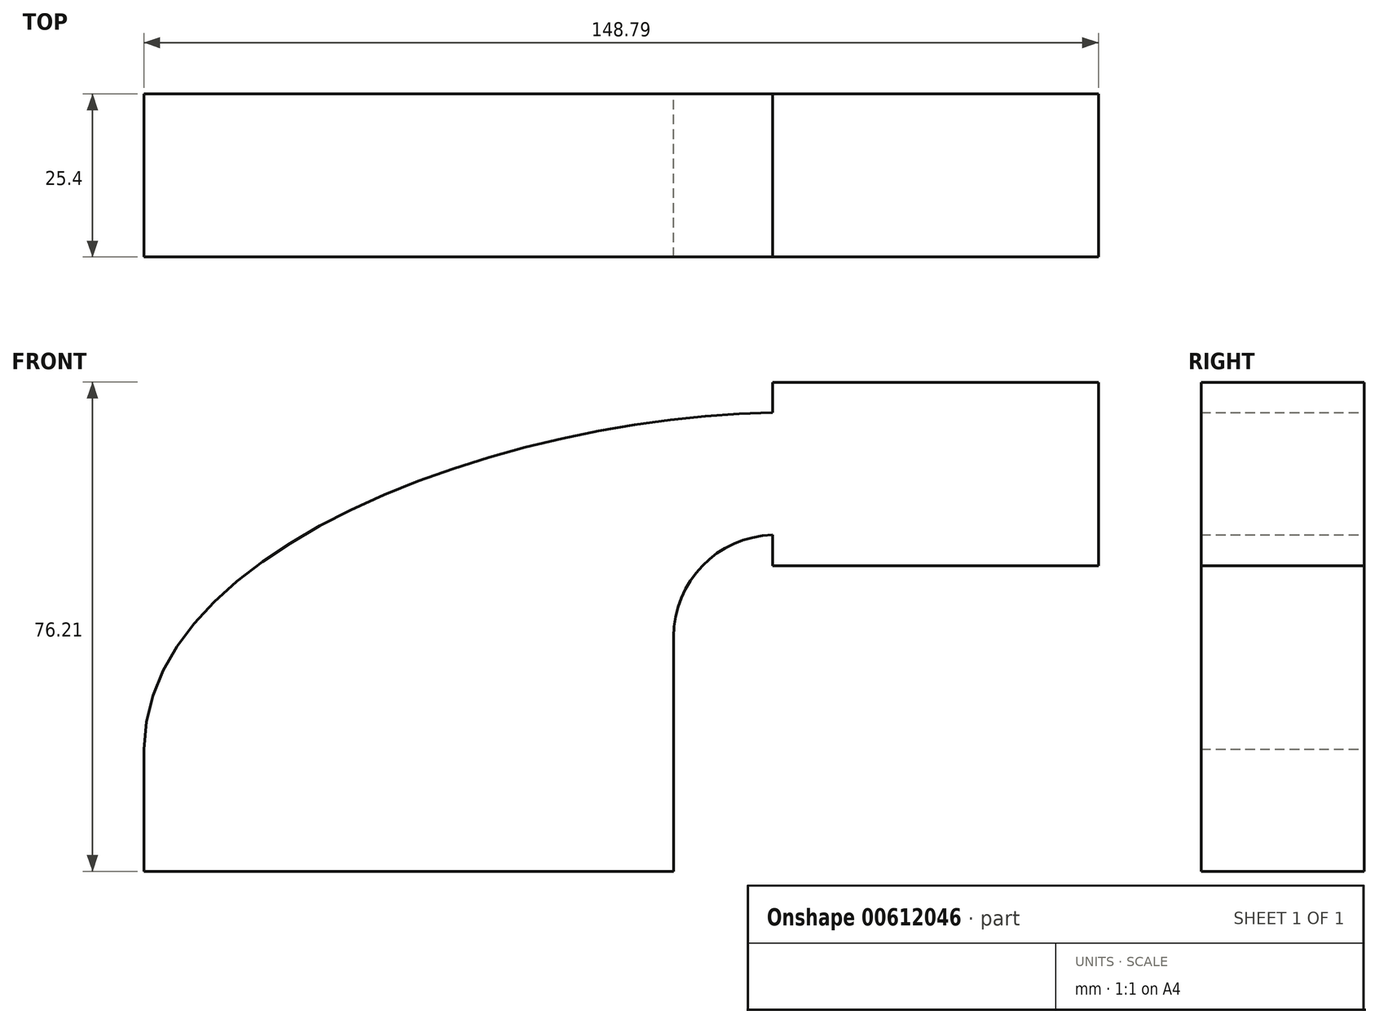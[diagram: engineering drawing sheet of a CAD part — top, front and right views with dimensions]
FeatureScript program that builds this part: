
annotation { "Feature Type Name" : "Feature", "Feature Type Description" : "" }
export const myFeature = defineFeature(function(context is Context, id is Id, definition is map)
    precondition{}
    {
        {
            var Q0;
            Q0=qCreatedBy(makeId("Front.planeOp"),FACE);
            var sketch = newSketch(context, id + "F0", { "sketchPlane" : qUnion([Q0])});
            skLineSegment(sketch, "E0.bottom", {"start": v(41.27, 9.53) * mm, "end": v(-41.28, 9.53) * mm});
            skLineSegment(sketch, "E0.top", {"start": v(41.28, -9.52) * mm, "end": v(-41.27, -9.52) * mm});
            skLineSegment(sketch, "E0.left", {"start": v(41.28, 9.53) * mm, "end": v(41.28, -9.52) * mm});
            skLineSegment(sketch, "E0.right", {"start": v(-41.28, 9.53) * mm, "end": v(-41.28, -9.52) * mm});
            skPoint(sketch, "E0.middle", {"position": v(0, 0) * mm});
            skLineSegment(sketch, "E1.bottom", {"start": v(107.5, 66.68) * mm, "end": v(56.7, 66.68) * mm});
            skLineSegment(sketch, "E1.top", {"start": v(107.5, 38.1) * mm, "end": v(56.7, 38.1) * mm});
            skLineSegment(sketch, "E1.left", {"start": v(107.5, 66.68) * mm, "end": v(107.5, 38.1) * mm});
            skLineSegment(sketch, "E1.right", {"start": v(56.7, 66.68) * mm, "end": v(56.7, 38.1) * mm});
            skPoint(sketch, "E1.middle", {"position": v(82.1, 52.39) * mm});
            skLineSegment(sketch, "E2", {"start": v(41.27, 9.53) * mm, "end": v(41.27, 27) * mm});
            skArc(sketch, "E3", {"start": v(41.27, 27) * mm, "mid": v(45.92, 38.23) * mm, "end": v(57.15, 42.88) * mm});
            skLineSegment(sketch, "E4", {"start": v(57.15, 42.88) * mm, "end": v(79.86, 42.88) * mm});
            skLineSegment(sketch, "E5.0", {"start": v(57.15, 61.93) * mm, "end": v(79.86, 61.93) * mm});
            skArc(sketch, "E5.1", {"start": v(22.22, 27) * mm, "mid": v(32.45, 51.7) * mm, "end": v(57.15, 61.93) * mm});
            skLineSegment(sketch, "E5.2", {"start": v(22.22, 9.53) * mm, "end": v(22.22, 27) * mm});
            skLineSegment(sketch, "E6", {"start": v(82.1, 38.1) * mm, "end": v(82.1, 66.68) * mm});
            skFitSpline(sketch, "E7", {"points": [v(-41.28, 9.53) * mm, v(57.15, 61.93) * mm], "startDerivative": vector(1.38, 99.69) * mm, "endDerivative": vector(114.16, 0.63) * mm});
            skSolve(sketch);
        }
        {
            var Q0;
            Q0 = qSketchRegion(id + "F0", true);
            extrude(context, id + "F1", {"entities" : qUnion([Q0]), "depth" : 25.4 * mm, "offsetDistance" : 25.4 * mm});
        }
    });
